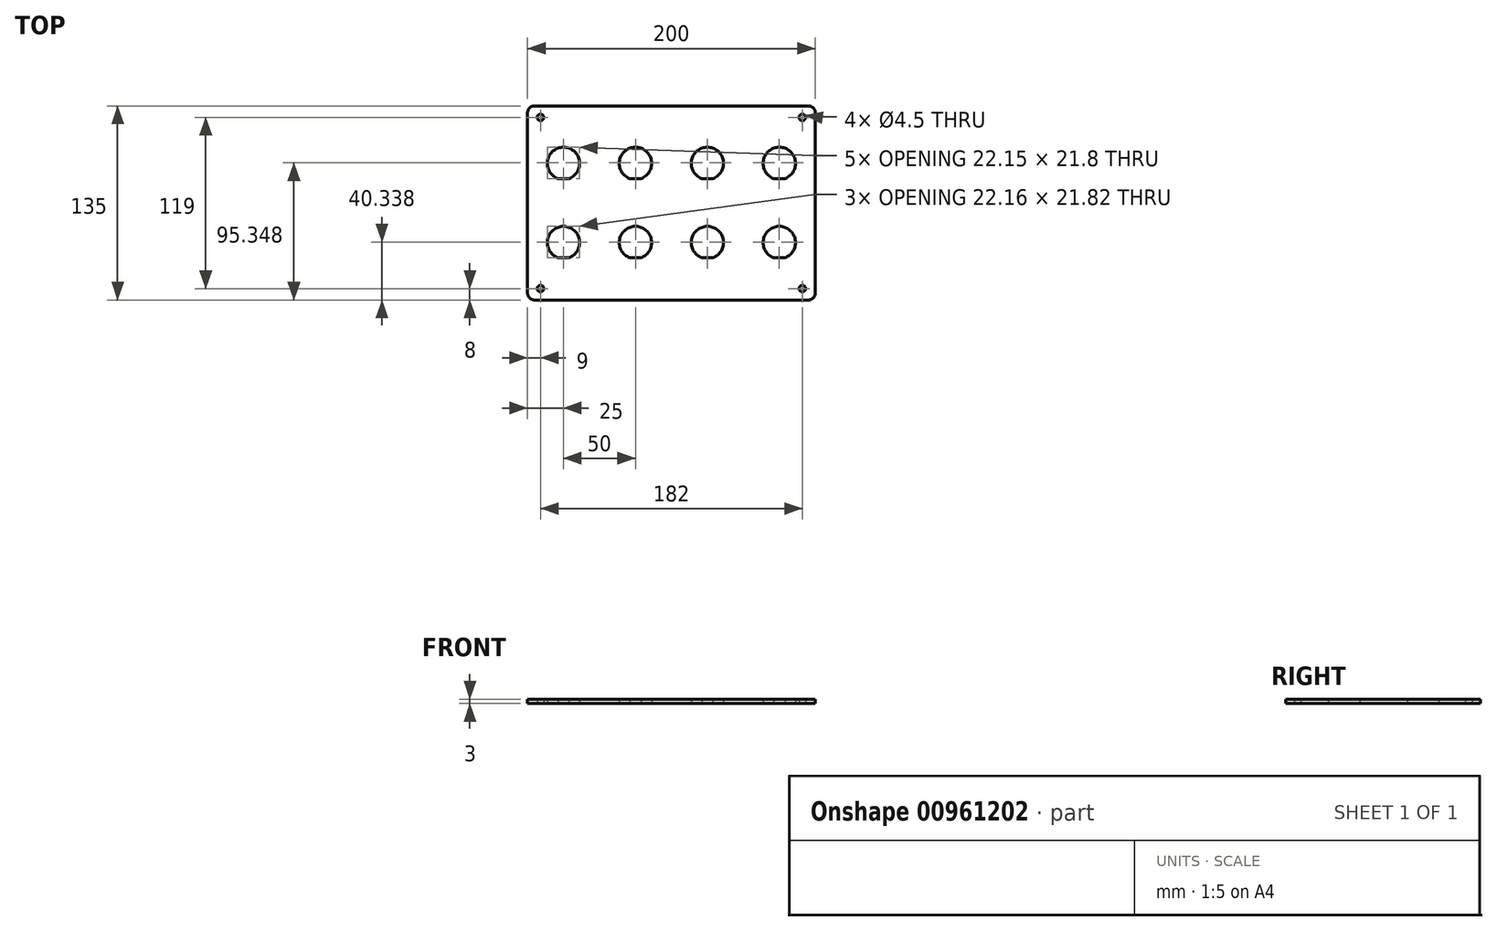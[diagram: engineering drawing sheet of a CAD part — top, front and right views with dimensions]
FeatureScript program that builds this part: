
annotation { "Feature Type Name" : "Feature", "Feature Type Description" : "" }
export const myFeature = defineFeature(function(context is Context, id is Id, definition is map)
    precondition{}
    {
        {
            var Q0;
            Q0=qCreatedBy(makeId("Top.planeOp"),FACE);
            var sketch = newSketch(context, id + "F0", { "sketchPlane" : qUnion([Q0])});
            skLineSegment(sketch, "E0.bottom", {"start": v(95, -67.5) * mm, "end": v(-95, -67.5) * mm});
            skLineSegment(sketch, "E0.top", {"start": v(95, 67.5) * mm, "end": v(-95, 67.5) * mm});
            skLineSegment(sketch, "E0.left", {"start": v(100, -62.5) * mm, "end": v(100, 62.5) * mm});
            skLineSegment(sketch, "E0.right", {"start": v(-100, -62.5) * mm, "end": v(-100, 62.5) * mm});
            skPoint(sketch, "E0.middle", {"position": v(0, 0) * mm});
            skPoint(sketch, "E1.visualSharp", {"position": v(-100, 67.5) * mm});
            skArc(sketch, "E1.filletArc", {"start": v(-95, 67.5) * mm, "mid": v(-98.54, 66.04) * mm, "end": v(-100, 62.5) * mm});
            skPoint(sketch, "E2.visualSharp", {"position": v(100, 67.5) * mm});
            skArc(sketch, "E2.filletArc", {"start": v(100, 62.5) * mm, "mid": v(98.54, 66.04) * mm, "end": v(95, 67.5) * mm});
            skPoint(sketch, "E3.visualSharp", {"position": v(100, -67.5) * mm});
            skArc(sketch, "E3.filletArc", {"start": v(95, -67.5) * mm, "mid": v(98.54, -66.04) * mm, "end": v(100, -62.5) * mm});
            skPoint(sketch, "E4.visualSharp", {"position": v(-100, -67.5) * mm});
            skArc(sketch, "E4.filletArc", {"start": v(-100, -62.5) * mm, "mid": v(-98.54, -66.04) * mm, "end": v(-95, -67.5) * mm});
            skArc(sketch, "E5", {"start": v(-71.1, 16.95) * mm, "mid": v(-75, 38.75) * mm, "end": v(-78.9, 16.95) * mm});
            skLineSegment(sketch, "E6", {"start": v(-71.1, 16.95) * mm, "end": v(-78.9, 16.95) * mm});
            skArc(sketch, "E7", {"start": v(-21.1, 16.95) * mm, "mid": v(-25, 38.75) * mm, "end": v(-28.9, 16.95) * mm});
            skLineSegment(sketch, "E8", {"start": v(-21.1, 16.95) * mm, "end": v(-28.9, 16.95) * mm});
            skArc(sketch, "E9", {"start": v(78.9, 16.95) * mm, "mid": v(75, 38.75) * mm, "end": v(71.1, 16.95) * mm});
            skLineSegment(sketch, "E10", {"start": v(78.9, 16.95) * mm, "end": v(71.1, 16.95) * mm});
            skArc(sketch, "E11", {"start": v(28.9, 16.95) * mm, "mid": v(25, 38.75) * mm, "end": v(21.1, 16.95) * mm});
            skLineSegment(sketch, "E12", {"start": v(28.9, 16.95) * mm, "end": v(21.1, 16.95) * mm});
            skArc(sketch, "E13", {"start": v(-71.16, -38.07) * mm, "mid": v(-75, -16.25) * mm, "end": v(-78.84, -38.07) * mm});
            skLineSegment(sketch, "E14", {"start": v(-71.16, -38.07) * mm, "end": v(-78.84, -38.07) * mm});
            skArc(sketch, "E15", {"start": v(-21.16, -38.07) * mm, "mid": v(-25, -16.25) * mm, "end": v(-28.84, -38.07) * mm});
            skLineSegment(sketch, "E16", {"start": v(-21.16, -38.07) * mm, "end": v(-28.84, -38.07) * mm});
            skArc(sketch, "E17", {"start": v(78.9, -38.05) * mm, "mid": v(75, -16.25) * mm, "end": v(71.1, -38.05) * mm});
            skLineSegment(sketch, "E18", {"start": v(78.9, -38.05) * mm, "end": v(71.1, -38.05) * mm});
            skArc(sketch, "E19", {"start": v(28.84, -38.07) * mm, "mid": v(25, -16.25) * mm, "end": v(21.16, -38.07) * mm});
            skLineSegment(sketch, "E20", {"start": v(28.84, -38.07) * mm, "end": v(21.16, -38.07) * mm});
            skCircle(sketch, "E21", {"center": v(-91, 59.5) * mm, "radius": 2.25 * mm});
            skCircle(sketch, "E22", {"center": v(91, 59.5) * mm, "radius": 2.25 * mm});
            skCircle(sketch, "E23", {"center": v(-91, -59.5) * mm, "radius": 2.25 * mm});
            skCircle(sketch, "E24", {"center": v(91, -59.5) * mm, "radius": 2.25 * mm});
            skLineSegment(sketch, "E25.0", {"start": v(95, 64) * mm, "end": v(-95, 64) * mm});
            skArc(sketch, "E25.1", {"start": v(96.5, 62.5) * mm, "mid": v(96.06, 63.56) * mm, "end": v(95, 64) * mm});
            skLineSegment(sketch, "E25.2", {"start": v(96.5, -62.5) * mm, "end": v(96.5, 62.5) * mm});
            skArc(sketch, "E26.0", {"start": v(95, -64) * mm, "mid": v(96.06, -63.56) * mm, "end": v(96.5, -62.5) * mm});
            skArc(sketch, "E26.1", {"start": v(-95, 64) * mm, "mid": v(-96.06, 63.56) * mm, "end": v(-96.5, 62.5) * mm});
            skLineSegment(sketch, "E26.2", {"start": v(-96.5, -62.5) * mm, "end": v(-96.5, 62.5) * mm});
            skArc(sketch, "E26.3", {"start": v(-96.5, -62.5) * mm, "mid": v(-96.06, -63.56) * mm, "end": v(-95, -64) * mm});
            skLineSegment(sketch, "E26.4", {"start": v(95, -64) * mm, "end": v(-95, -64) * mm});
            skCircle(sketch, "E27", {"center": v(-75, 27.5) * mm, "radius": 15.5 * mm, "construction": true});
            skCircle(sketch, "E28", {"center": v(-75, -27.5) * mm, "radius": 15.5 * mm, "construction": true});
            skCircle(sketch, "E29", {"center": v(-91, 59.5) * mm, "radius": 4.5 * mm, "construction": true});
            skCircle(sketch, "E30", {"center": v(-91, -59.5) * mm, "radius": 4.5 * mm, "construction": true});
            skLineSegment(sketch, "E31.bottom", {"start": v(-87.5, 45) * mm, "end": v(-62.5, 45) * mm});
            skLineSegment(sketch, "E31.top", {"start": v(-87.5, 0) * mm, "end": v(-62.5, 0) * mm});
            skLineSegment(sketch, "E31.left", {"start": v(-92.5, 40) * mm, "end": v(-92.5, 5) * mm});
            skLineSegment(sketch, "E31.right", {"start": v(-57.5, 40) * mm, "end": v(-57.5, 5) * mm});
            skLineSegment(sketch, "E32.bottom", {"start": v(-37.5, 45) * mm, "end": v(-12.5, 45) * mm});
            skLineSegment(sketch, "E32.top", {"start": v(-37.5, 0) * mm, "end": v(-12.5, 0) * mm});
            skLineSegment(sketch, "E32.left", {"start": v(-42.5, 40) * mm, "end": v(-42.5, 5) * mm});
            skLineSegment(sketch, "E32.right", {"start": v(-7.5, 40) * mm, "end": v(-7.5, 5) * mm});
            skPoint(sketch, "E33.visualSharp", {"position": v(-92.5, 45) * mm});
            skArc(sketch, "E33.filletArc", {"start": v(-87.5, 45) * mm, "mid": v(-91.04, 43.54) * mm, "end": v(-92.5, 40) * mm});
            skPoint(sketch, "E34.visualSharp", {"position": v(-57.5, 45) * mm});
            skArc(sketch, "E34.filletArc", {"start": v(-57.5, 40) * mm, "mid": v(-58.96, 43.54) * mm, "end": v(-62.5, 45) * mm});
            skPoint(sketch, "E35.visualSharp", {"position": v(-92.5, 0) * mm});
            skArc(sketch, "E35.filletArc", {"start": v(-92.5, 5) * mm, "mid": v(-91.04, 1.46) * mm, "end": v(-87.5, 0) * mm});
            skPoint(sketch, "E36.visualSharp", {"position": v(-57.5, 0) * mm});
            skArc(sketch, "E36.filletArc", {"start": v(-62.5, 0) * mm, "mid": v(-58.96, 1.46) * mm, "end": v(-57.5, 5) * mm});
            skPoint(sketch, "E37.visualSharp", {"position": v(-42.5, 0) * mm});
            skArc(sketch, "E37.filletArc", {"start": v(-42.5, 5) * mm, "mid": v(-41.04, 1.46) * mm, "end": v(-37.5, 0) * mm});
            skPoint(sketch, "E38.visualSharp", {"position": v(-42.5, 45) * mm});
            skArc(sketch, "E38.filletArc", {"start": v(-37.5, 45) * mm, "mid": v(-41.04, 43.54) * mm, "end": v(-42.5, 40) * mm});
            skPoint(sketch, "E39.visualSharp", {"position": v(-7.5, 45) * mm});
            skArc(sketch, "E39.filletArc", {"start": v(-7.5, 40) * mm, "mid": v(-8.96, 43.54) * mm, "end": v(-12.5, 45) * mm});
            skPoint(sketch, "E40.visualSharp", {"position": v(-7.5, 0) * mm});
            skArc(sketch, "E40.filletArc", {"start": v(-12.5, 0) * mm, "mid": v(-8.96, 1.46) * mm, "end": v(-7.5, 5) * mm});
            skLineSegment(sketch, "E41.bottom", {"start": v(12.5, 45) * mm, "end": v(37.5, 45) * mm});
            skLineSegment(sketch, "E41.top", {"start": v(12.5, 0) * mm, "end": v(37.5, 0) * mm});
            skLineSegment(sketch, "E41.left", {"start": v(7.5, 40) * mm, "end": v(7.5, 5) * mm});
            skLineSegment(sketch, "E41.right", {"start": v(42.5, 40) * mm, "end": v(42.5, 5) * mm});
            skLineSegment(sketch, "E42.bottom", {"start": v(62.5, 45) * mm, "end": v(87.5, 45) * mm});
            skLineSegment(sketch, "E42.top", {"start": v(62.5, 0) * mm, "end": v(87.5, 0) * mm});
            skLineSegment(sketch, "E42.left", {"start": v(57.5, 40) * mm, "end": v(57.5, 5) * mm});
            skLineSegment(sketch, "E42.right", {"start": v(92.5, 40) * mm, "end": v(92.5, 5) * mm});
            skLineSegment(sketch, "E43.bottom", {"start": v(-87.5, -10) * mm, "end": v(-62.5, -10) * mm});
            skLineSegment(sketch, "E43.top", {"start": v(-87.5, -55) * mm, "end": v(-62.5, -55) * mm});
            skLineSegment(sketch, "E43.left", {"start": v(-92.5, -15) * mm, "end": v(-92.5, -50) * mm});
            skLineSegment(sketch, "E43.right", {"start": v(-57.5, -15) * mm, "end": v(-57.5, -50) * mm});
            skLineSegment(sketch, "E44.bottom", {"start": v(-37.5, -10) * mm, "end": v(-12.5, -10) * mm});
            skLineSegment(sketch, "E44.top", {"start": v(-37.5, -55) * mm, "end": v(-12.5, -55) * mm});
            skLineSegment(sketch, "E44.left", {"start": v(-42.5, -15) * mm, "end": v(-42.5, -50) * mm});
            skLineSegment(sketch, "E44.right", {"start": v(-7.5, -15) * mm, "end": v(-7.5, -50) * mm});
            skLineSegment(sketch, "E45.bottom", {"start": v(12.5, -10) * mm, "end": v(37.5, -10) * mm});
            skLineSegment(sketch, "E45.top", {"start": v(12.5, -55) * mm, "end": v(37.5, -55) * mm});
            skLineSegment(sketch, "E45.left", {"start": v(7.5, -15) * mm, "end": v(7.5, -50) * mm});
            skLineSegment(sketch, "E45.right", {"start": v(42.5, -15) * mm, "end": v(42.5, -50) * mm});
            skLineSegment(sketch, "E46.bottom", {"start": v(62.5, -10) * mm, "end": v(87.5, -10) * mm});
            skLineSegment(sketch, "E46.top", {"start": v(62.5, -55) * mm, "end": v(87.5, -55) * mm});
            skLineSegment(sketch, "E46.left", {"start": v(57.5, -15) * mm, "end": v(57.5, -50) * mm});
            skLineSegment(sketch, "E46.right", {"start": v(92.5, -15) * mm, "end": v(92.5, -50) * mm});
            skPoint(sketch, "E47.visualSharp", {"position": v(7.5, 45) * mm});
            skArc(sketch, "E47.filletArc", {"start": v(12.5, 45) * mm, "mid": v(8.96, 43.54) * mm, "end": v(7.5, 40) * mm});
            skPoint(sketch, "E48.visualSharp", {"position": v(42.5, 45) * mm});
            skArc(sketch, "E48.filletArc", {"start": v(42.5, 40) * mm, "mid": v(41.04, 43.54) * mm, "end": v(37.5, 45) * mm});
            skPoint(sketch, "E49.visualSharp", {"position": v(57.5, 45) * mm});
            skArc(sketch, "E49.filletArc", {"start": v(62.5, 45) * mm, "mid": v(58.96, 43.54) * mm, "end": v(57.5, 40) * mm});
            skPoint(sketch, "E50.visualSharp", {"position": v(92.5, 45) * mm});
            skArc(sketch, "E50.filletArc", {"start": v(92.5, 40) * mm, "mid": v(91.04, 43.54) * mm, "end": v(87.5, 45) * mm});
            skPoint(sketch, "E51.visualSharp", {"position": v(57.5, 0) * mm});
            skArc(sketch, "E51.filletArc", {"start": v(57.5, 5) * mm, "mid": v(58.96, 1.46) * mm, "end": v(62.5, 0) * mm});
            skPoint(sketch, "E52.visualSharp", {"position": v(92.5, 0) * mm});
            skArc(sketch, "E52.filletArc", {"start": v(87.5, 0) * mm, "mid": v(91.04, 1.46) * mm, "end": v(92.5, 5) * mm});
            skPoint(sketch, "E53.visualSharp", {"position": v(-92.5, -10) * mm});
            skArc(sketch, "E53.filletArc", {"start": v(-87.5, -10) * mm, "mid": v(-91.04, -11.46) * mm, "end": v(-92.5, -15) * mm});
            skPoint(sketch, "E54.visualSharp", {"position": v(-57.5, -10) * mm});
            skArc(sketch, "E54.filletArc", {"start": v(-57.5, -15) * mm, "mid": v(-58.96, -11.46) * mm, "end": v(-62.5, -10) * mm});
            skPoint(sketch, "E55.visualSharp", {"position": v(-57.5, -55) * mm});
            skArc(sketch, "E55.filletArc", {"start": v(-62.5, -55) * mm, "mid": v(-58.96, -53.54) * mm, "end": v(-57.5, -50) * mm});
            skPoint(sketch, "E56.visualSharp", {"position": v(-92.5, -55) * mm});
            skArc(sketch, "E56.filletArc", {"start": v(-92.5, -50) * mm, "mid": v(-91.04, -53.54) * mm, "end": v(-87.5, -55) * mm});
            skPoint(sketch, "E57.visualSharp", {"position": v(-42.5, -55) * mm});
            skArc(sketch, "E57.filletArc", {"start": v(-42.5, -50) * mm, "mid": v(-41.04, -53.54) * mm, "end": v(-37.5, -55) * mm});
            skPoint(sketch, "E58.visualSharp", {"position": v(-7.5, -55) * mm});
            skArc(sketch, "E58.filletArc", {"start": v(-12.5, -55) * mm, "mid": v(-8.96, -53.54) * mm, "end": v(-7.5, -50) * mm});
            skPoint(sketch, "E59.visualSharp", {"position": v(-7.5, -10) * mm});
            skArc(sketch, "E59.filletArc", {"start": v(-7.5, -15) * mm, "mid": v(-8.96, -11.46) * mm, "end": v(-12.5, -10) * mm});
            skPoint(sketch, "E60.visualSharp", {"position": v(-42.5, -10) * mm});
            skArc(sketch, "E60.filletArc", {"start": v(-37.5, -10) * mm, "mid": v(-41.04, -11.46) * mm, "end": v(-42.5, -15) * mm});
            skPoint(sketch, "E61.visualSharp", {"position": v(7.5, -10) * mm});
            skArc(sketch, "E61.filletArc", {"start": v(12.5, -10) * mm, "mid": v(8.96, -11.46) * mm, "end": v(7.5, -15) * mm});
            skPoint(sketch, "E62.visualSharp", {"position": v(42.5, -10) * mm});
            skArc(sketch, "E62.filletArc", {"start": v(42.5, -15) * mm, "mid": v(41.04, -11.46) * mm, "end": v(37.5, -10) * mm});
            skPoint(sketch, "E63.visualSharp", {"position": v(7.5, -55) * mm});
            skArc(sketch, "E63.filletArc", {"start": v(7.5, -50) * mm, "mid": v(8.96, -53.54) * mm, "end": v(12.5, -55) * mm});
            skPoint(sketch, "E64.visualSharp", {"position": v(42.5, -55) * mm});
            skArc(sketch, "E64.filletArc", {"start": v(37.5, -55) * mm, "mid": v(41.04, -53.54) * mm, "end": v(42.5, -50) * mm});
            skPoint(sketch, "E65.visualSharp", {"position": v(57.5, -55) * mm});
            skArc(sketch, "E65.filletArc", {"start": v(57.5, -50) * mm, "mid": v(58.96, -53.54) * mm, "end": v(62.5, -55) * mm});
            skPoint(sketch, "E66.visualSharp", {"position": v(57.5, -10) * mm});
            skArc(sketch, "E66.filletArc", {"start": v(62.5, -10) * mm, "mid": v(58.96, -11.46) * mm, "end": v(57.5, -15) * mm});
            skPoint(sketch, "E67.visualSharp", {"position": v(92.5, -10) * mm});
            skArc(sketch, "E67.filletArc", {"start": v(92.5, -15) * mm, "mid": v(91.04, -11.46) * mm, "end": v(87.5, -10) * mm});
            skPoint(sketch, "E68.visualSharp", {"position": v(92.5, -55) * mm});
            skArc(sketch, "E68.filletArc", {"start": v(87.5, -55) * mm, "mid": v(91.04, -53.54) * mm, "end": v(92.5, -50) * mm});
            skPoint(sketch, "E69.visualSharp", {"position": v(7.5, 0) * mm});
            skArc(sketch, "E69.filletArc", {"start": v(7.5, 5) * mm, "mid": v(8.96, 1.46) * mm, "end": v(12.5, 0) * mm});
            skPoint(sketch, "E70.visualSharp", {"position": v(42.5, 0) * mm});
            skArc(sketch, "E70.filletArc", {"start": v(37.5, 0) * mm, "mid": v(41.04, 1.46) * mm, "end": v(42.5, 5) * mm});
            skSolve(sketch);
        }
        {
            var Q0;
            Q0=makeQuery(id+"F0.imprint","IMPRINT",FACE,{"disambiguationData":[TD([[makeQuery(id+"F0.imprint","IMPRINT",EDGE,{"derivedFrom":sQuery(id+"F0.wireOp",EDGE,"E9")}),-1.0]])]});
            var Q1;
            Q1=makeQuery(id+"F0.imprint","IMPRINT",FACE,{"disambiguationData":[TD([[makeQuery(id+"F0.imprint","IMPRINT",EDGE,{"derivedFrom":sQuery(id+"F0.wireOp",EDGE,"E5")}),-1.0]])]});
            var Q2;
            Q2=makeQuery(id+"F0.imprint","IMPRINT",FACE,{"disambiguationData":[TD([[makeQuery(id+"F0.imprint","IMPRINT",EDGE,{"derivedFrom":sQuery(id+"F0.wireOp",EDGE,"E7")}),-1.0]])]});
            var Q3;
            Q3=makeQuery(id+"F0.imprint","IMPRINT",FACE,{"disambiguationData":[TD([[makeQuery(id+"F0.imprint","IMPRINT",EDGE,{"derivedFrom":sQuery(id+"F0.wireOp",EDGE,"E0.bottom")}),-1.0]])]});
            var Q4;
            Q4=makeQuery(id+"F0.imprint","IMPRINT",FACE,{"disambiguationData":[TD([[makeQuery(id+"F0.imprint","IMPRINT",EDGE,{"derivedFrom":sQuery(id+"F0.wireOp",EDGE,"E11")}),-1.0]])]});
            var Q5;
            Q5=makeQuery(id+"F0.imprint","IMPRINT",FACE,{"disambiguationData":[TD([[makeQuery(id+"F0.imprint","IMPRINT",EDGE,{"derivedFrom":sQuery(id+"F0.wireOp",EDGE,"E13")}),-1.0]])]});
            var Q6;
            Q6=makeQuery(id+"F0.imprint","IMPRINT",FACE,{"disambiguationData":[TD([[makeQuery(id+"F0.imprint","IMPRINT",EDGE,{"derivedFrom":sQuery(id+"F0.wireOp",EDGE,"E15")}),-1.0]])]});
            var Q7;
            Q7=makeQuery(id+"F0.imprint","IMPRINT",FACE,{"disambiguationData":[TD([[makeQuery(id+"F0.imprint","IMPRINT",EDGE,{"derivedFrom":sQuery(id+"F0.wireOp",EDGE,"E17")}),-1.0]])]});
            var Q8;
            Q8=makeQuery(id+"F0.imprint","IMPRINT",FACE,{"disambiguationData":[TD([[makeQuery(id+"F0.imprint","IMPRINT",EDGE,{"derivedFrom":sQuery(id+"F0.wireOp",EDGE,"E19")}),-1.0]])]});
            var Q9;
            Q9=makeQuery(id+"F0.imprint","IMPRINT",FACE,{"disambiguationData":[TD([[makeQuery(id+"F0.imprint","IMPRINT",EDGE,{"derivedFrom":sQuery(id+"F0.wireOp",EDGE,"E21")}),-1.0]])]});
            extrude(context, id + "F1", {"entities" : qUnion([Q0, Q1, Q2, Q3, Q4, Q5, Q6, Q7, Q8, Q9]), "depth" : 3 * mm, "offsetDistance" : 25 * mm});
        }
    });
